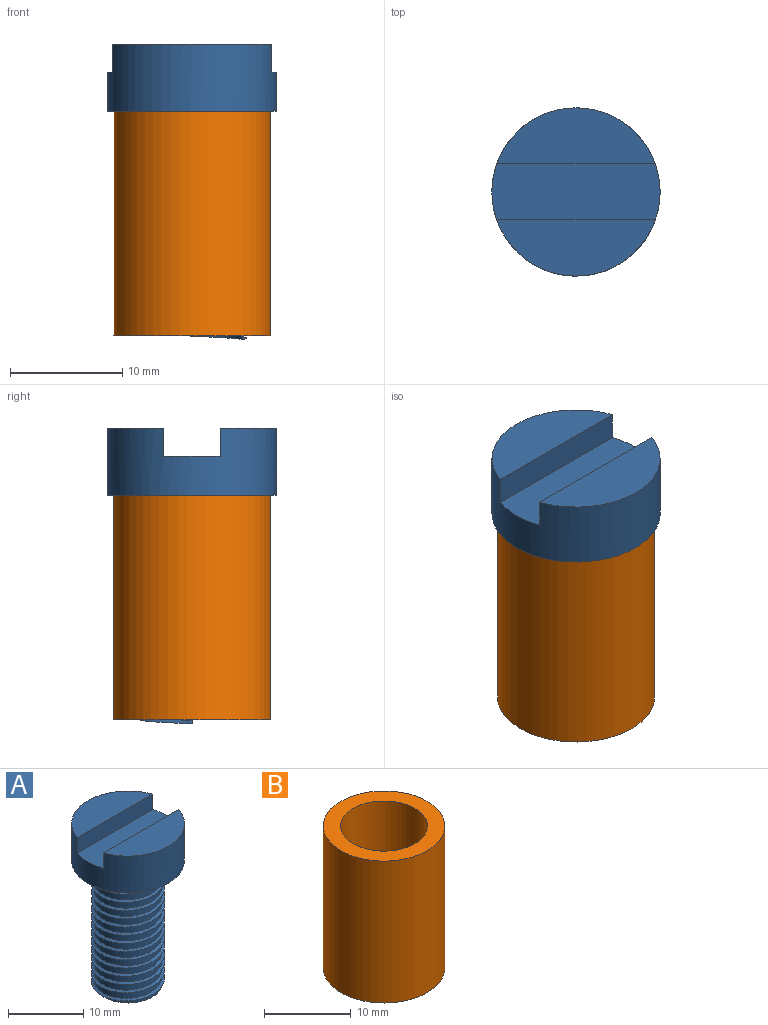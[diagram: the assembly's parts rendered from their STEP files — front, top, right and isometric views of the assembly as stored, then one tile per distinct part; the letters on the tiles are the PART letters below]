
ASSEMBLY  parts=2 mates=1
PART A: 29 faces, bbox 15x15x26.4 mm
  f0: plane 14.14x5mm, normal (0,0,1), area 51.6mm2, adj f17,f27
  f1: cylinder r=4.5mm len=9mm, axis (0,0,1), area 20.7mm2, adj f2,f19,f23,f24
  f2: cylinder r=4.5mm len=9mm, axis (0,0,1), area 29.2mm2, adj f1,f3,f24,f25
  f3: cylinder r=4.5mm len=9mm, axis (0,0,1), area 29.2mm2, adj f2,f4,f24,f25
  f4: cylinder r=4.5mm len=9mm, axis (0,0,1), area 29.2mm2, adj f3,f5,f24,f25
  f5: cylinder r=4.5mm len=9mm, axis (0,0,1), area 29.2mm2, adj f4,f6,f24,f25
  f6: cylinder r=4.5mm len=9mm, axis (0,0,1), area 29.2mm2, adj f5,f7,f24,f25
  f7: cylinder r=4.5mm len=9mm, axis (0,0,1), area 29.2mm2, adj f6,f8,f24,f25
  f8: cylinder r=4.5mm len=9mm, axis (0,0,1), area 29.2mm2, adj f7,f9,f24,f25
  f9: cylinder r=4.5mm len=9mm, axis (0,0,1), area 29.2mm2, adj f8,f10,f24,f25
  f10: cylinder r=4.5mm len=9mm, axis (0,0,1), area 29.2mm2, adj f9,f11,f24,f25
  f11: cylinder r=4.5mm len=9mm, axis (0,0,1), area 29.2mm2, adj f10,f12,f24,f25
  f12: cylinder r=4.5mm len=9mm, axis (0,0,1), area 29.2mm2, adj f11,f13,f24,f25
  f13: cylinder r=4.5mm len=9mm, axis (0,0,1), area 29.2mm2, adj f12,f14,f24,f25
  f14: cylinder r=4.5mm len=9mm, axis (0,0,1), area 29.2mm2, adj f13,f15,f24,f25
  f15: cylinder r=4.5mm len=9mm, axis (0,0,1), area 29.2mm2, adj f14,f16,f20,f24,f25
  f16: cylinder r=4.5mm len=9mm, axis (0,0,1), area 10mm2, adj f15,f20,f25
  f17: cylinder r=7.5mm len=15mm, axis (0,0,-1), area 257.3mm2, adj f0,f18,f19,f26,f27,f28
  f18: plane 14.14x5mm, normal (0,0,1), area 51.6mm2, adj f17,f26
  f19: plane 15x15mm, normal (0,0,-1), area 113.1mm2, adj f1,f17
  f20: plane 9x9mm, normal (0,0,-1), area 63.6mm2, adj f15,f16,f21
  f21: cylinder r=4.5mm len=5.13mm, axis (0,0,1), area 1.4mm2, adj f20,f22,f24,f25
  f22: plane 0.37x0.3mm, normal (0,-1,0), area 0.1mm2, adj f21,f24,f25
  f23: plane 0.37x0.3mm, normal (0,1,0), area 0.1mm2, adj f1,f24,f25
  f24: bspline ~20.15x11.25mm, area 176.3mm2, adj f1,f2,f3,f4,f5,f6,f7,f8
  f25: bspline ~20.15x11.25mm, area 176.8mm2, adj f2,f3,f4,f5,f6,f7,f8,f9
  f26: plane 14.14x2.5mm, normal (0,-1,0), area 35.4mm2, adj f17,f18,f28
  f27: plane 14.14x2.5mm, normal (0,1,0), area 35.4mm2, adj f0,f17,f28
  f28: plane 15x5mm, normal (0,0,1), area 73.6mm2, adj f17,f26,f27
PART B: 4 faces, bbox 14x14x20 mm
  f0: cylinder r=5mm len=20mm, axis (0,0,-1), area 628.3mm2, adj f2,f3
  f1: cylinder r=7mm len=20mm, axis (0,0,-1), area 879.6mm2, adj f2,f3
  f2: plane 14x14mm, normal (0,0,1), area 75.4mm2, adj f0,f1
  f3: plane 14x14mm, normal (0,0,-1), area 75.4mm2, adj f0,f1
PLACE A t=(-42.95,-42.49,11.13)mm
PLACE B t=(-2.43,5.73,-8.87)mm
MATE slider A.f1 <-> B.f0  axis (0,0,-1) through (-42.95,-42.49,-8.87)mm
